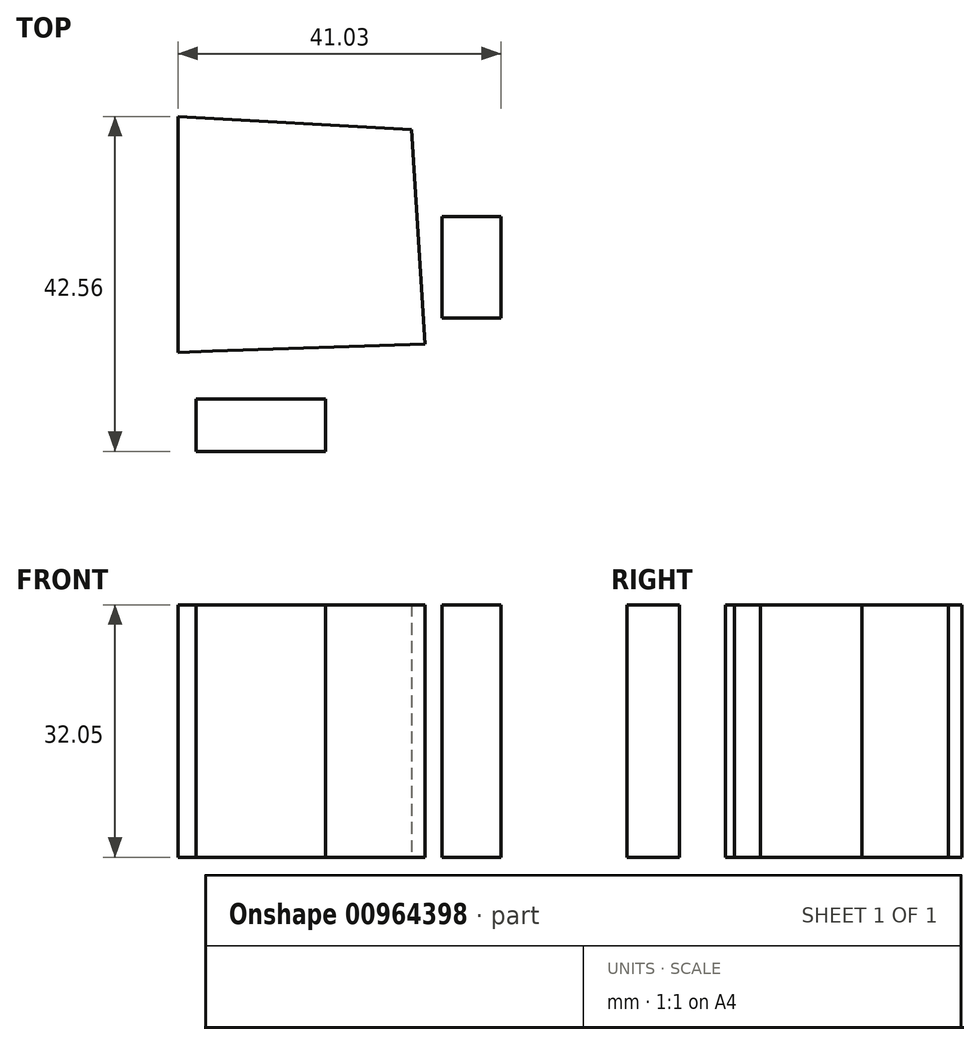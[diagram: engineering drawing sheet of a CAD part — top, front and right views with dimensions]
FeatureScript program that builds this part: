
annotation { "Feature Type Name" : "Feature", "Feature Type Description" : "" }
export const myFeature = defineFeature(function(context is Context, id is Id, definition is map)
    precondition{}
    {
        {
            var Q0;
            Q0=qCreatedBy(makeId("Top.planeOp"),FACE);
            var sketch = newSketch(context, id + "F0", { "sketchPlane" : qUnion([Q0])});
            skLineSegment(sketch, "E0", {"start": v(9.8, 14.54) * mm, "end": v(9.8, 44.57) * mm});
            skLineSegment(sketch, "E1", {"start": v(9.8, 44.57) * mm, "end": v(39.44, 42.86) * mm});
            skLineSegment(sketch, "E2", {"start": v(39.44, 42.86) * mm, "end": v(41.16, 15.67) * mm});
            skLineSegment(sketch, "E3", {"start": v(41.16, 15.67) * mm, "end": v(14.16, 14.73) * mm});
            skLineSegment(sketch, "E4", {"start": v(9.8, 14.54) * mm, "end": v(14.16, 14.73) * mm});
            skLineSegment(sketch, "E5.bottom", {"start": v(50.84, 18.93) * mm, "end": v(43.33, 18.93) * mm});
            skLineSegment(sketch, "E5.top", {"start": v(50.84, 31.81) * mm, "end": v(43.33, 31.81) * mm});
            skLineSegment(sketch, "E5.left", {"start": v(50.84, 18.93) * mm, "end": v(50.84, 31.81) * mm});
            skLineSegment(sketch, "E5.right", {"start": v(43.33, 18.93) * mm, "end": v(43.33, 31.81) * mm});
            skLineSegment(sketch, "E6.bottom", {"start": v(12.1, 8.67) * mm, "end": v(28.51, 8.67) * mm});
            skLineSegment(sketch, "E6.top", {"start": v(12.1, 2.01) * mm, "end": v(28.51, 2.01) * mm});
            skLineSegment(sketch, "E6.left", {"start": v(12.1, 8.67) * mm, "end": v(12.1, 2.01) * mm});
            skLineSegment(sketch, "E6.right", {"start": v(28.51, 8.67) * mm, "end": v(28.51, 2.01) * mm});
            skSolve(sketch);
        }
        {
            var Q0;
            Q0 = qSketchRegion(id + "F0", true);
            extrude(context, id + "F1", {"entities" : qUnion([Q0]), "depth" : 32.05 * mm, "offsetDistance" : 25.4 * mm});
        }
    });
